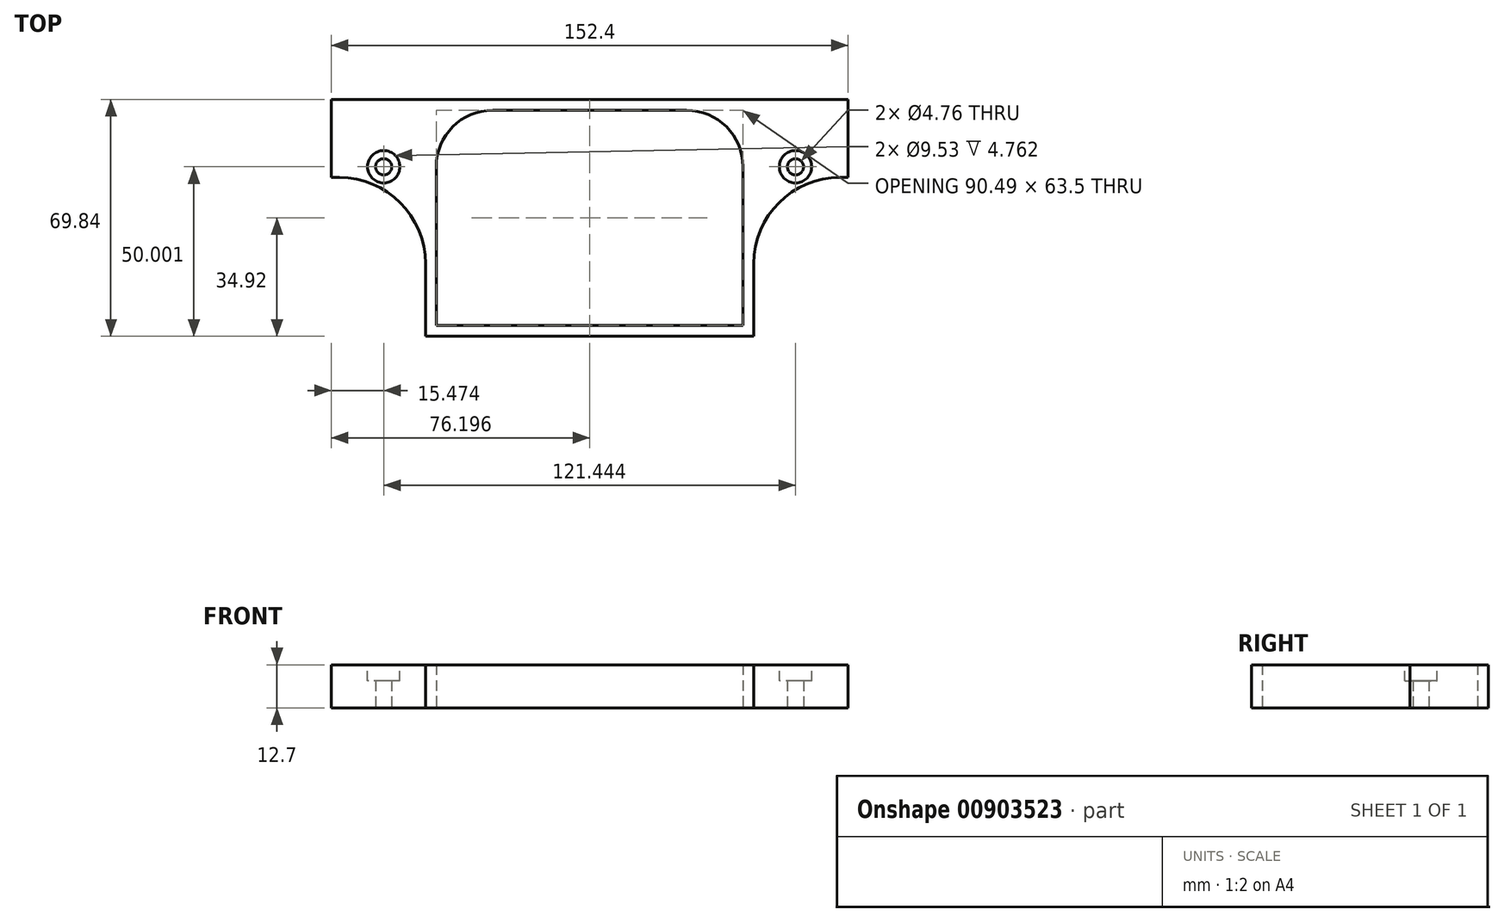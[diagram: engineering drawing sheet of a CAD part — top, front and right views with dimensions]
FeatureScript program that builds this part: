
annotation { "Feature Type Name" : "Feature", "Feature Type Description" : "" }
export const myFeature = defineFeature(function(context is Context, id is Id, definition is map)
    precondition{}
    {
        {
            var Q0;
            Q0=qCreatedBy(makeId("Top.planeOp"),FACE);
            var sketch = newSketch(context, id + "F0", { "sketchPlane" : qUnion([Q0])});
            skLineSegment(sketch, "E0.bottom", {"start": v(0, 0) * mm, "end": v(-90.49, 0) * mm});
            skLineSegment(sketch, "E0.top", {"start": v(-16.67, 63.5) * mm, "end": v(-73.82, 63.5) * mm});
            skLineSegment(sketch, "E0.left", {"start": v(0, 0) * mm, "end": v(0, 46.83) * mm});
            skLineSegment(sketch, "E0.right", {"start": v(-90.49, 0) * mm, "end": v(-90.49, 46.83) * mm});
            skPoint(sketch, "E1.visualSharp", {"position": v(-90.49, 63.5) * mm});
            skArc(sketch, "E1.filletArc", {"start": v(-73.82, 63.5) * mm, "mid": v(-85.6, 58.62) * mm, "end": v(-90.49, 46.83) * mm});
            skPoint(sketch, "E2.visualSharp", {"position": v(0, 63.5) * mm});
            skArc(sketch, "E2.filletArc", {"start": v(0, 46.83) * mm, "mid": v(-4.88, 58.62) * mm, "end": v(-16.67, 63.5) * mm});
            skLineSegment(sketch, "E3.bottom", {"start": v(30.96, 66.68) * mm, "end": v(-121.44, 66.67) * mm});
            skLineSegment(sketch, "E3.top", {"start": v(3.17, -3.17) * mm, "end": v(-93.66, -3.18) * mm});
            skLineSegment(sketch, "E3.left", {"start": v(30.96, 66.68) * mm, "end": v(30.96, 43.66) * mm});
            skLineSegment(sketch, "E3.right", {"start": v(-121.44, 66.67) * mm, "end": v(-121.44, 43.66) * mm});
            skLineSegment(sketch, "E4", {"start": v(-121.44, 46.83) * mm, "end": v(-90.49, 46.83) * mm});
            skLineSegment(sketch, "E5", {"start": v(0, 46.83) * mm, "end": v(30.96, 46.83) * mm});
            skCircle(sketch, "E6", {"center": v(-105.97, 46.83) * mm, "radius": 2.38 * mm});
            skCircle(sketch, "E7", {"center": v(15.48, 46.83) * mm, "radius": 2.38 * mm});
            skLineSegment(sketch, "E8", {"start": v(-93.66, -3.18) * mm, "end": v(-93.66, 18.26) * mm});
            skLineSegment(sketch, "E9", {"start": v(-119.06, 43.66) * mm, "end": v(-121.44, 43.66) * mm});
            skLineSegment(sketch, "E10", {"start": v(3.18, -3.17) * mm, "end": v(3.18, 18.26) * mm});
            skLineSegment(sketch, "E11", {"start": v(28.58, 43.66) * mm, "end": v(30.96, 43.66) * mm});
            skPoint(sketch, "E12.visualSharp", {"position": v(-93.66, 43.66) * mm});
            skArc(sketch, "E12.filletArc", {"start": v(-93.66, 18.26) * mm, "mid": v(-101.1, 36.22) * mm, "end": v(-119.06, 43.66) * mm});
            skPoint(sketch, "E13.visualSharp", {"position": v(3.18, 43.66) * mm});
            skArc(sketch, "E13.filletArc", {"start": v(28.58, 43.66) * mm, "mid": v(10.61, 36.22) * mm, "end": v(3.18, 18.26) * mm});
            skSolve(sketch);
        }
        {
            var Q0;
            Q0=makeQuery(id+"F0.imprint","IMPRINT",FACE,{"disambiguationData":[TD([[makeQuery(id+"F0.imprint","IMPRINT",EDGE,{"derivedFrom":sQuery(id+"F0.wireOp",EDGE,"E0.top")}),-1.0]])]});
            var Q1;
            {var subQ2=sQuery(id+"F0.wireOp",EDGE,"E0.bottom");Q1=makeQuery(id+"F0.imprint","IMPRINT",FACE,{"disambiguationData":[TD([[makeQuery(id+"F0.imprint","IMPRINT",EDGE,{"derivedFrom":subQ2}),1.0]])]});}
            extrude(context, id + "F1", {"entities" : qUnion([Q0, Q1]), "depth" : 12.7 * mm, "offsetDistance" : 25.4 * mm});
        }
        {
            var Q0;
            Q0=makeQuery(id+"F1.opExtrude","CAP_FACE",FACE,{"disambiguationData":[OSD([sQuery(id+"F0.wireOp",EDGE,"E0.bottom"),sQuery(id+"F0.wireOp",EDGE,"E0.top"),sQuery(id+"F0.wireOp",EDGE,"E0.left"),sQuery(id+"F0.wireOp",EDGE,"E0.right"),sQuery(id+"F0.wireOp",EDGE,"E1.filletArc"),sQuery(id+"F0.wireOp",EDGE,"E2.filletArc"),sQuery(id+"F0.wireOp",EDGE,"E3.bottom"),sQuery(id+"F0.wireOp",EDGE,"E3.top"),sQuery(id+"F0.wireOp",EDGE,"E3.left"),sQuery(id+"F0.wireOp",EDGE,"E3.right"),sQuery(id+"F0.wireOp",EDGE,"E6"),sQuery(id+"F0.wireOp",EDGE,"E7"),sQuery(id+"F0.wireOp",EDGE,"E8"),sQuery(id+"F0.wireOp",EDGE,"E9"),sQuery(id+"F0.wireOp",EDGE,"E10"),sQuery(id+"F0.wireOp",EDGE,"E11"),sQuery(id+"F0.wireOp",EDGE,"E12.filletArc"),sQuery(id+"F0.wireOp",EDGE,"E13.filletArc")])],"isStart":false});
            var Q1;
            Q1=makeQuery(id+"F1.opExtrude","CAP_FACE",FACE,{"disambiguationData":[OSD([sQuery(id+"F0.wireOp",EDGE,"E0.bottom"),sQuery(id+"F0.wireOp",EDGE,"E0.top"),sQuery(id+"F0.wireOp",EDGE,"E0.left"),sQuery(id+"F0.wireOp",EDGE,"E0.right"),sQuery(id+"F0.wireOp",EDGE,"E1.filletArc"),sQuery(id+"F0.wireOp",EDGE,"E2.filletArc"),sQuery(id+"F0.wireOp",EDGE,"E3.bottom"),sQuery(id+"F0.wireOp",EDGE,"E3.top"),sQuery(id+"F0.wireOp",EDGE,"E3.left"),sQuery(id+"F0.wireOp",EDGE,"E3.right"),sQuery(id+"F0.wireOp",EDGE,"E6"),sQuery(id+"F0.wireOp",EDGE,"E7"),sQuery(id+"F0.wireOp",EDGE,"E8"),sQuery(id+"F0.wireOp",EDGE,"E9"),sQuery(id+"F0.wireOp",EDGE,"E10"),sQuery(id+"F0.wireOp",EDGE,"E11"),sQuery(id+"F0.wireOp",EDGE,"E12.filletArc"),sQuery(id+"F0.wireOp",EDGE,"E13.filletArc")])],"isStart":false});
            var sketch = newSketch(context, id + "F2", { "sketchPlane" : qUnion([Q0, Q1])});
            skCircle(sketch, "E14.0", {"center": v(-105.97, 46.83) * mm, "radius": 2.38 * mm});
            skCircle(sketch, "E15.0", {"center": v(15.48, 46.83) * mm, "radius": 2.38 * mm});
            skCircle(sketch, "E16", {"center": v(-105.97, 46.83) * mm, "radius": 4.76 * mm});
            skCircle(sketch, "E17", {"center": v(15.48, 46.83) * mm, "radius": 4.76 * mm});
            skSolve(sketch);
        }
        {
            var Q0;
            Q0 = qSketchRegion(id + "F2", true);
            var Q1;
            Q1=makeQuery(id+"F2.imprint","IMPRINT",FACE,{"disambiguationData":[TD([[makeQuery(id+"F2.imprint","IMPRINT",EDGE,{"derivedFrom":sQuery(id+"F2.wireOp",EDGE,"E14.0")}),-1.0]])]});
            var Q2;
            Q2=makeQuery(id+"F2.imprint","IMPRINT",FACE,{"disambiguationData":[TD([[makeQuery(id+"F2.imprint","IMPRINT",EDGE,{"derivedFrom":sQuery(id+"F2.wireOp",EDGE,"E15.0")}),-1.0]])]});
            extrude(context, id + "F3", {"entities" : qUnion([Q0, Q1, Q2]), "operationType" : NewBodyOperationType.REMOVE, "oppositeDirection" : true, "depth" : 4.76 * mm, "offsetDistance" : 25.4 * mm});
        }
    });
